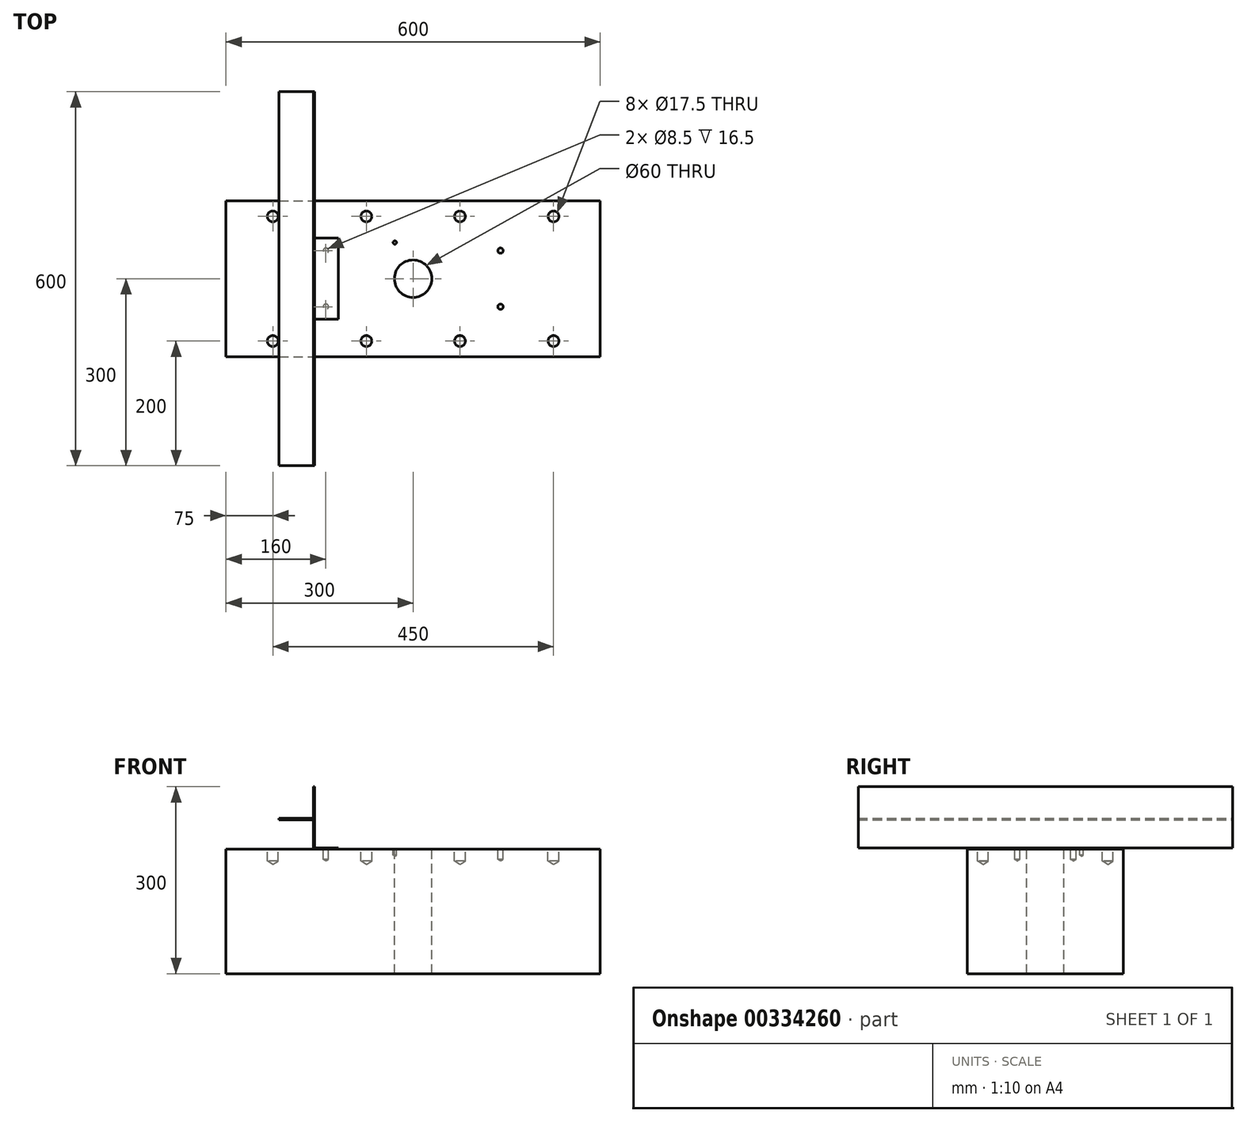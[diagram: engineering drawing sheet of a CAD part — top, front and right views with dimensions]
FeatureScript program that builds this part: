
annotation { "Feature Type Name" : "Feature", "Feature Type Description" : "" }
export const myFeature = defineFeature(function(context is Context, id is Id, definition is map)
    precondition{}
    {
        {
            var Q0;
            Q0=qCreatedBy(makeId("Top.planeOp"),FACE);
            var sketch = newSketch(context, id + "F0", { "sketchPlane" : qUnion([Q0])});
            skLineSegment(sketch, "E0.bottom", {"start": v(-300, 125) * mm, "end": v(300, 125) * mm});
            skLineSegment(sketch, "E0.top", {"start": v(-300, -125) * mm, "end": v(300, -125) * mm});
            skLineSegment(sketch, "E0.left", {"start": v(-300, 125) * mm, "end": v(-300, -125) * mm});
            skLineSegment(sketch, "E0.right", {"start": v(300, 125) * mm, "end": v(300, -125) * mm});
            skPoint(sketch, "E0.middle", {"position": v(0, 0) * mm});
            skCircle(sketch, "E1", {"center": v(0, 0) * mm, "radius": 30 * mm});
            skSolve(sketch);
        }
        {
            var Q0;
            Q0 = qSketchRegion(id + "F0", true);
            extrude(context, id + "F1", {"entities" : qUnion([Q0]), "oppositeDirection" : true, "depth" : 200 * mm});
        }
        {
            var Q0;
            Q0=makeQuery(id+"F1.opExtrude","CAP_FACE",FACE,{"disambiguationData":[OSD([sQuery(id+"F0.wireOp",EDGE,"E0.bottom"),sQuery(id+"F0.wireOp",EDGE,"E0.top"),sQuery(id+"F0.wireOp",EDGE,"E0.left"),sQuery(id+"F0.wireOp",EDGE,"E0.right"),sQuery(id+"F0.wireOp",EDGE,"E1")])],"isStart":true});
            var sketch = newSketch(context, id + "F2", { "sketchPlane" : qUnion([Q0])});
            skPoint(sketch, "E2", {"position": v(-29.34, 58) * mm});
            skSolve(sketch);
        }
        {
            var Q0;
            Q0=sQuery(id+"F2.wireOp",VERTEX,"E2");
            var Q1;
            Q1=makeQuery(id+"F1.opExtrude","SWEPT_BODY",BODY,{"disambiguationData":[OSD([sQuery(id+"F0.wireOp",EDGE,"E0.bottom"),sQuery(id+"F0.wireOp",EDGE,"E0.top"),sQuery(id+"F0.wireOp",EDGE,"E0.left"),sQuery(id+"F0.wireOp",EDGE,"E0.right"),sQuery(id+"F0.wireOp",EDGE,"E1")])]});
            hole(context, id + "F3", {"style" : HoleStyle.SIMPLE, "endStyle" : HoleEndStyle.BLIND, "standardTappedOrClearance" : lookupTablePath({ "standard" : "ISO", "fit" : "Normal", "size" : "M5", "type" : "Clearance" }), "standardBlindInLast" : lookupTablePath({ "fit" : "Standard", "standard" : "ISO", "size" : "M5", "type" : "Clearance" }), "holeDiameter" : 5.5 * mm, "holeDepth" : 10 * mm, "tappedDepth" : 12 * mm, "tapClearance" : 3, "locations" : qUnion([Q0]), "scope" : qUnion([Q1])});
        }
        {
            var Q0;
            Q0=makeQuery(id+"F1.opExtrude","CAP_FACE",FACE,{"disambiguationData":[OSD([sQuery(id+"F0.wireOp",EDGE,"E0.bottom"),sQuery(id+"F0.wireOp",EDGE,"E0.top"),sQuery(id+"F0.wireOp",EDGE,"E0.left"),sQuery(id+"F0.wireOp",EDGE,"E0.right"),sQuery(id+"F0.wireOp",EDGE,"E1")])],"isStart":true});
            var sketch = newSketch(context, id + "F4", { "sketchPlane" : qUnion([Q0])});
            skPoint(sketch, "E3.middle", {"position": v(0, 0) * mm});
            skLineSegment(sketch, "E4.bottom", {"start": v(-225, 100) * mm, "end": v(225, 100) * mm, "construction": true});
            skLineSegment(sketch, "E4.top", {"start": v(-225, -100) * mm, "end": v(225, -100) * mm, "construction": true});
            skLineSegment(sketch, "E4.left", {"start": v(-225, 100) * mm, "end": v(-225, -100) * mm, "construction": true});
            skLineSegment(sketch, "E4.right", {"start": v(225, 100) * mm, "end": v(225, -100) * mm, "construction": true});
            skPoint(sketch, "E5", {"position": v(-75, 100) * mm});
            skPoint(sketch, "E6", {"position": v(75, 100) * mm});
            skPoint(sketch, "E7", {"position": v(75, -100) * mm});
            skPoint(sketch, "E8", {"position": v(-75, -100) * mm});
            skLineSegment(sketch, "E9", {"start": v(-75, 100) * mm, "end": v(-75, -100) * mm, "construction": true});
            skLineSegment(sketch, "E10", {"start": v(75, 100) * mm, "end": v(75, -100) * mm, "construction": true});
            skSolve(sketch);
        }
        {
            var Q0;
            Q0=sQuery(id+"F4.wireOp",VERTEX,"E4.left.start");
            var Q1;
            Q1=sQuery(id+"F4.wireOp",VERTEX,"E4.left.end");
            var Q2;
            Q2=sQuery(id+"F4.wireOp",VERTEX,"E4.right.start");
            var Q3;
            Q3=sQuery(id+"F4.wireOp",VERTEX,"E4.right.end");
            var Q4;
            Q4=sQuery(id+"F4.wireOp",VERTEX,"E6");
            var Q5;
            Q5=sQuery(id+"F4.wireOp",VERTEX,"E8");
            var Q6;
            Q6=sQuery(id+"F4.wireOp",VERTEX,"E7");
            var Q7;
            Q7=sQuery(id+"F4.wireOp",VERTEX,"E5");
            var Q8;
            Q8=makeQuery(id+"F1.opExtrude","SWEPT_BODY",BODY,{"disambiguationData":[OSD([sQuery(id+"F0.wireOp",EDGE,"E0.bottom"),sQuery(id+"F0.wireOp",EDGE,"E0.top"),sQuery(id+"F0.wireOp",EDGE,"E0.left"),sQuery(id+"F0.wireOp",EDGE,"E0.right"),sQuery(id+"F0.wireOp",EDGE,"E1")])]});
            hole(context, id + "F5", {"style" : HoleStyle.SIMPLE, "endStyle" : HoleEndStyle.BLIND, "standardTappedOrClearance" : lookupTablePath({ "standard" : "ISO", "engagement" : "75%", "pitch" : "2.5 mm", "size" : "M20", "type" : "Tapped" }), "standardBlindInLast" : lookupTablePath({ "standard" : "ISO", "engagement" : "75%", "pitch" : "2.5 mm", "size" : "M20", "type" : "Tapped" }), "holeDiameter" : 17.5 * mm, "showTappedDepth" : true, "holeDepth" : 19.5 * mm, "tappedDepth" : 12 * mm, "tapClearance" : 3, "locations" : qUnion([Q0, Q1, Q2, Q3, Q4, Q5, Q6, Q7]), "scope" : qUnion([Q8]), "majorDiameter" : 20 * mm});
        }
        {
            var Q0;
            Q0=makeQuery(id+"F4.imprint","IMPRINT",FACE,{"disambiguationData":[TD([[makeQuery(id+"F4.imprint","IMPRINT",EDGE,{"derivedFrom":makeQuery(id+"F1.opExtrude","CAP_EDGE",EDGE,{"disambiguationData":[OSD([sQuery(id+"F0.wireOp",EDGE,"E0.bottom")])],"isStart":true})}),-1.0]])]});
            var sketch = newSketch(context, id + "F6", { "sketchPlane" : qUnion([Q0])});
            skLineSegment(sketch, "E11.bottom", {"start": v(-140, 45) * mm, "end": v(140, 45) * mm, "construction": true});
            skLineSegment(sketch, "E11.top", {"start": v(-140, -45) * mm, "end": v(140, -45) * mm, "construction": true});
            skLineSegment(sketch, "E11.left", {"start": v(-140, 45) * mm, "end": v(-140, -45) * mm, "construction": true});
            skLineSegment(sketch, "E11.right", {"start": v(140, 45) * mm, "end": v(140, -45) * mm, "construction": true});
            skPoint(sketch, "E11.middle", {"position": v(0, 0) * mm});
            skSolve(sketch);
        }
        {
            var Q0;
            Q0=sQuery(id+"F6.wireOp",VERTEX,"E11.left.start");
            var Q1;
            Q1=sQuery(id+"F6.wireOp",VERTEX,"E11.left.end");
            var Q2;
            Q2=sQuery(id+"F6.wireOp",VERTEX,"E11.top.end");
            var Q3;
            Q3=sQuery(id+"F6.wireOp",VERTEX,"E11.right.start");
            var Q4;
            Q4=makeQuery(id+"F1.opExtrude","SWEPT_BODY",BODY,{"disambiguationData":[OSD([sQuery(id+"F0.wireOp",EDGE,"E0.bottom"),sQuery(id+"F0.wireOp",EDGE,"E0.top"),sQuery(id+"F0.wireOp",EDGE,"E0.left"),sQuery(id+"F0.wireOp",EDGE,"E0.right"),sQuery(id+"F0.wireOp",EDGE,"E1")])]});
            hole(context, id + "F7", {"style" : HoleStyle.SIMPLE, "endStyle" : HoleEndStyle.BLIND, "standardTappedOrClearance" : lookupTablePath({ "standard" : "ISO", "engagement" : "75%", "pitch" : "1.5 mm", "size" : "M10", "type" : "Tapped" }), "standardBlindInLast" : lookupTablePath({ "standard" : "ISO", "engagement" : "75%", "pitch" : "1.5 mm", "size" : "M10", "type" : "Tapped" }), "holeDiameter" : 8.5 * mm, "showTappedDepth" : true, "holeDepth" : 16.5 * mm, "tappedDepth" : 12 * mm, "tapClearance" : 3, "locations" : qUnion([Q0, Q1, Q2, Q3]), "scope" : qUnion([Q4]), "majorDiameter" : 10 * mm});
        }
        {
            var Q0;
            Q0=makeQuery(id+"F1.opExtrude","CAP_FACE",FACE,{"disambiguationData":[OSD([sQuery(id+"F0.wireOp",EDGE,"E0.bottom"),sQuery(id+"F0.wireOp",EDGE,"E0.top"),sQuery(id+"F0.wireOp",EDGE,"E0.left"),sQuery(id+"F0.wireOp",EDGE,"E0.right"),sQuery(id+"F0.wireOp",EDGE,"E1")])],"isStart":true});
            var sketch = newSketch(context, id + "F8", { "sketchPlane" : qUnion([Q0])});
            skLineSegment(sketch, "E12.bottom", {"start": v(-160, 65) * mm, "end": v(-120, 65) * mm});
            skLineSegment(sketch, "E12.top", {"start": v(-160, -65) * mm, "end": v(-120, -65) * mm});
            skLineSegment(sketch, "E12.left", {"start": v(-160, 65) * mm, "end": v(-160, -65) * mm});
            skLineSegment(sketch, "E12.right", {"start": v(-120, 65) * mm, "end": v(-120, -65) * mm});
            skPoint(sketch, "E12.middle", {"position": v(-140, 0) * mm});
            skLineSegment(sketch, "E13", {"start": v(-140, 45) * mm, "end": v(-140, -45) * mm});
            skSolve(sketch);
        }
        {
            var Q0;
            Q0 = qSketchRegion(id + "F8", true);
            extrude(context, id + "F9", {"entities" : qUnion([Q0]), "operationType" : NewBodyOperationType.ADD, "depth" : 2 * mm});
        }
        {
            var Q0;
            Q0=qCreatedBy(makeId("Front.planeOp"),FACE);
            var sketch = newSketch(context, id + "F10", { "sketchPlane" : qUnion([Q0])});
            skLineSegment(sketch, "E14.bottom", {"start": v(-160, 100) * mm, "end": v(-158, 100) * mm});
            skLineSegment(sketch, "E14.top", {"start": v(-160, 2) * mm, "end": v(-158, 2) * mm});
            skLineSegment(sketch, "E14.right", {"start": v(-158, 100) * mm, "end": v(-158, 2) * mm});
            skLineSegment(sketch, "E15", {"start": v(-160, 100) * mm, "end": v(-160, 49) * mm});
            skLineSegment(sketch, "E16", {"start": v(-160, 49) * mm, "end": v(-215, 49) * mm});
            skLineSegment(sketch, "E17", {"start": v(-215, 49) * mm, "end": v(-215, 47) * mm});
            skLineSegment(sketch, "E18", {"start": v(-215, 47) * mm, "end": v(-160, 47) * mm});
            skLineSegment(sketch, "E19", {"start": v(-160, 47) * mm, "end": v(-160, 2) * mm});
            skSolve(sketch);
        }
        {
            var Q0;
            Q0 = qSketchRegion(id + "F10", true);
            var Q1;
            Q1=makeQuery(id+"F9.opExtrude","SWEPT_FACE",FACE,{"disambiguationData":[OSD([sQuery(id+"F8.wireOp",EDGE,"E12.top")])]});
            var Q2;
            Q2=makeQuery(id+"F9.opExtrude","SWEPT_FACE",FACE,{"disambiguationData":[OSD([sQuery(id+"F8.wireOp",EDGE,"E12.bottom")])]});
            extrude(context, id + "F11", {"entities" : qUnion([Q0]), "operationType" : NewBodyOperationType.ADD, "endBound" : BoundingType.SYMMETRIC, "endBoundEntityFace" : qUnion([Q1]), "depth" : 600 * mm, "hasSecondDirection" : true, "secondDirectionOppositeDirection" : true, "secondDirectionBoundEntityFace" : qUnion([Q2]), "secondDirectionDepth" : 200 * mm});
        }
    });
